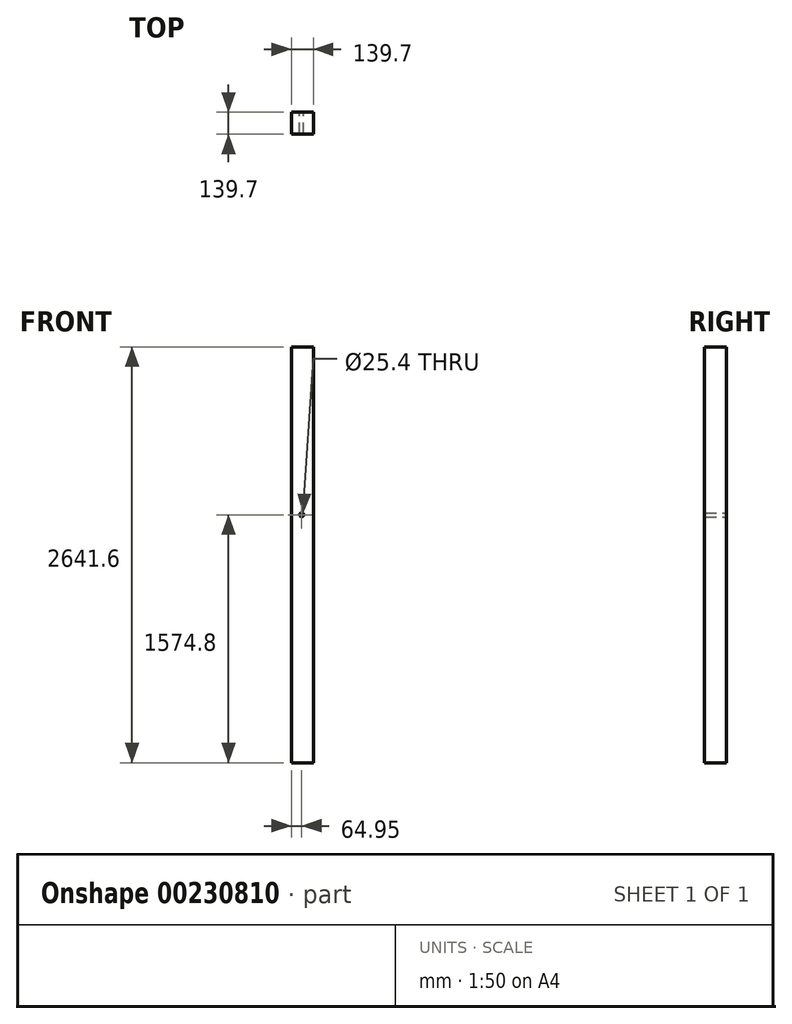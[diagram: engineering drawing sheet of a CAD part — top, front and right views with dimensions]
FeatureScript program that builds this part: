
annotation { "Feature Type Name" : "Feature", "Feature Type Description" : "" }
export const myFeature = defineFeature(function(context is Context, id is Id, definition is map)
    precondition{}
    {
        {
            var Q0;
            Q0=qCreatedBy(makeId("Front.planeOp"),FACE);
            var sketch = newSketch(context, id + "F0", { "sketchPlane" : qUnion([Q0])});
            skLineSegment(sketch, "E0.bottom", {"start": v(-64.95, 1066.8) * mm, "end": v(74.75, 1066.8) * mm});
            skLineSegment(sketch, "E0.top", {"start": v(-64.95, -1574.8) * mm, "end": v(74.75, -1574.8) * mm});
            skLineSegment(sketch, "E0.left", {"start": v(-64.95, 1066.8) * mm, "end": v(-64.95, -1574.8) * mm});
            skLineSegment(sketch, "E0.right", {"start": v(74.75, 1066.8) * mm, "end": v(74.75, -1574.8) * mm});
            skCircle(sketch, "E1", {"center": v(0, 0) * mm, "radius": 12.7 * mm});
            skSolve(sketch);
        }
        {
            var Q0;
            Q0=makeQuery(id+"F0.imprint","IMPRINT",FACE,{"disambiguationData":[TD([[makeQuery(id+"F0.imprint","IMPRINT",EDGE,{"derivedFrom":sQuery(id+"F0.wireOp",EDGE,"E0.bottom")}),-1.0]])]});
            extrude(context, id + "F1", {"entities" : qUnion([Q0]), "depth" : 139.7 * mm});
        }
    });
